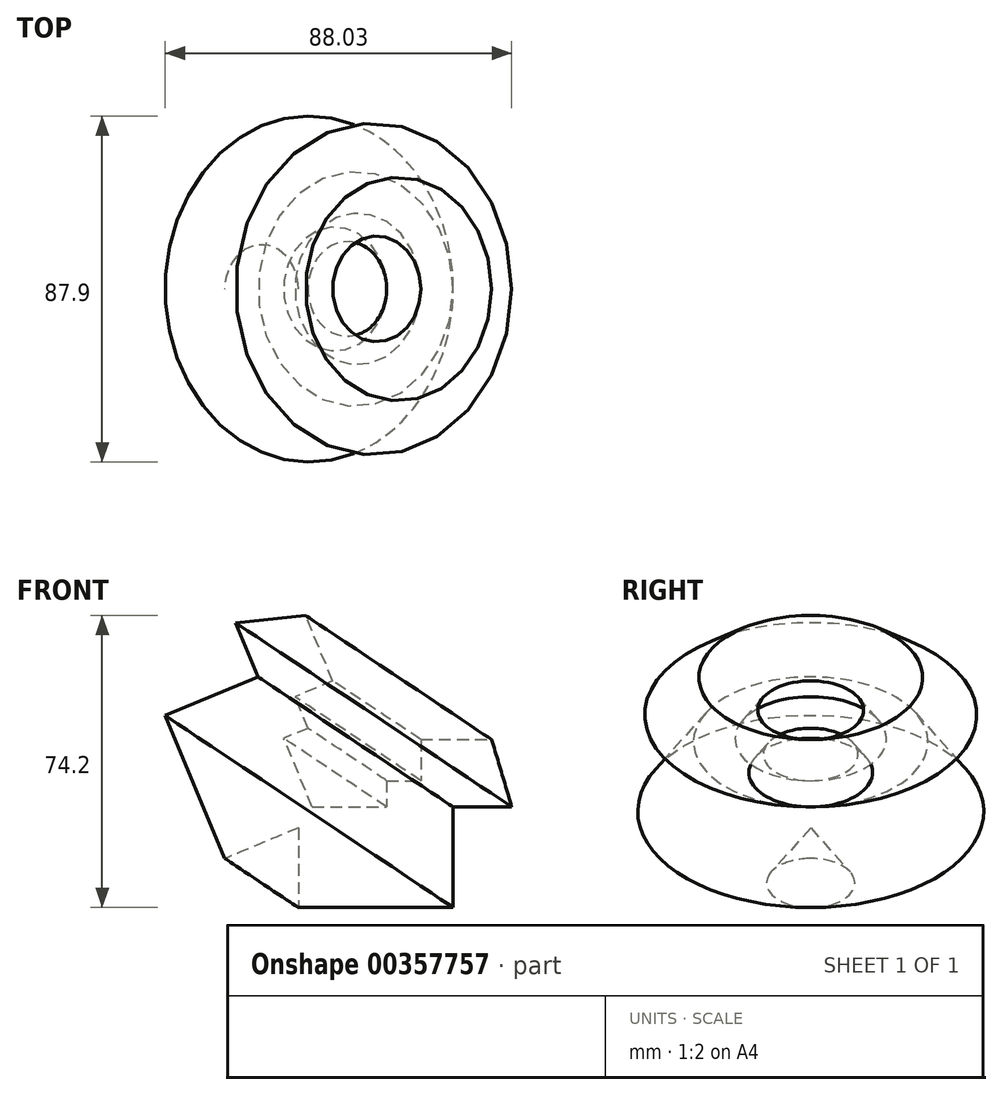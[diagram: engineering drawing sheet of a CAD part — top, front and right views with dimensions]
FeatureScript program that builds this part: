
annotation { "Feature Type Name" : "Feature", "Feature Type Description" : "" }
export const myFeature = defineFeature(function(context is Context, id is Id, definition is map)
    precondition{}
    {
        {
            var Q0;
            Q0=qCreatedBy(makeId("Front.planeOp"),FACE);
            var sketch = newSketch(context, id + "F0", { "sketchPlane" : qUnion([Q0])});
            skLineSegment(sketch, "E0", {"start": v(0, 20.22) * mm, "end": v(0, 0) * mm});
            skLineSegment(sketch, "E1", {"start": v(39.34, 0) * mm, "end": v(39.34, 25.56) * mm});
            skLineSegment(sketch, "E2", {"start": v(39.34, 25.56) * mm, "end": v(54.23, 25.56) * mm});
            skLineSegment(sketch, "E3", {"start": v(54.23, 25.56) * mm, "end": v(49.12, 42.67) * mm});
            skLineSegment(sketch, "E4", {"start": v(49.12, 42.67) * mm, "end": v(31.12, 42.67) * mm});
            skLineSegment(sketch, "E5", {"start": v(31.12, 42.67) * mm, "end": v(31.12, 32.23) * mm});
            skLineSegment(sketch, "E6", {"start": v(31.12, 32.23) * mm, "end": v(22.45, 32.23) * mm});
            skLineSegment(sketch, "E7", {"start": v(22.45, 32.23) * mm, "end": v(22.45, 25.56) * mm});
            skLineSegment(sketch, "E8", {"start": v(22.45, 25.56) * mm, "end": v(3.56, 25.56) * mm});
            skLineSegment(sketch, "E9", {"start": v(3.56, 25.56) * mm, "end": v(0, 20.22) * mm});
            skLineSegment(sketch, "E10", {"start": v(18, 0) * mm, "end": v(0, 0) * mm});
            skLineSegment(sketch, "E11", {"start": v(18, 0) * mm, "end": v(39.34, 0) * mm});
            skSolve(sketch);
        }
        {
            var Q0;
            Q0=makeQuery(id+"F0.imprint","IMPRINT",FACE,{"disambiguationData":[TD([[makeQuery(id+"F0.imprint","IMPRINT",EDGE,{"derivedFrom":sQuery(id+"F0.wireOp",EDGE,"E0")}),1.0]])]});
            var Q1;
            Q1=sQuery(id+"F0.wireOp",EDGE,"E9");
            revolve(context, id + "F1", {"entities" : qUnion([Q0]), "axis" : qUnion([Q1]), "revolveType" : RevolveType.FULL});
        }
    });
